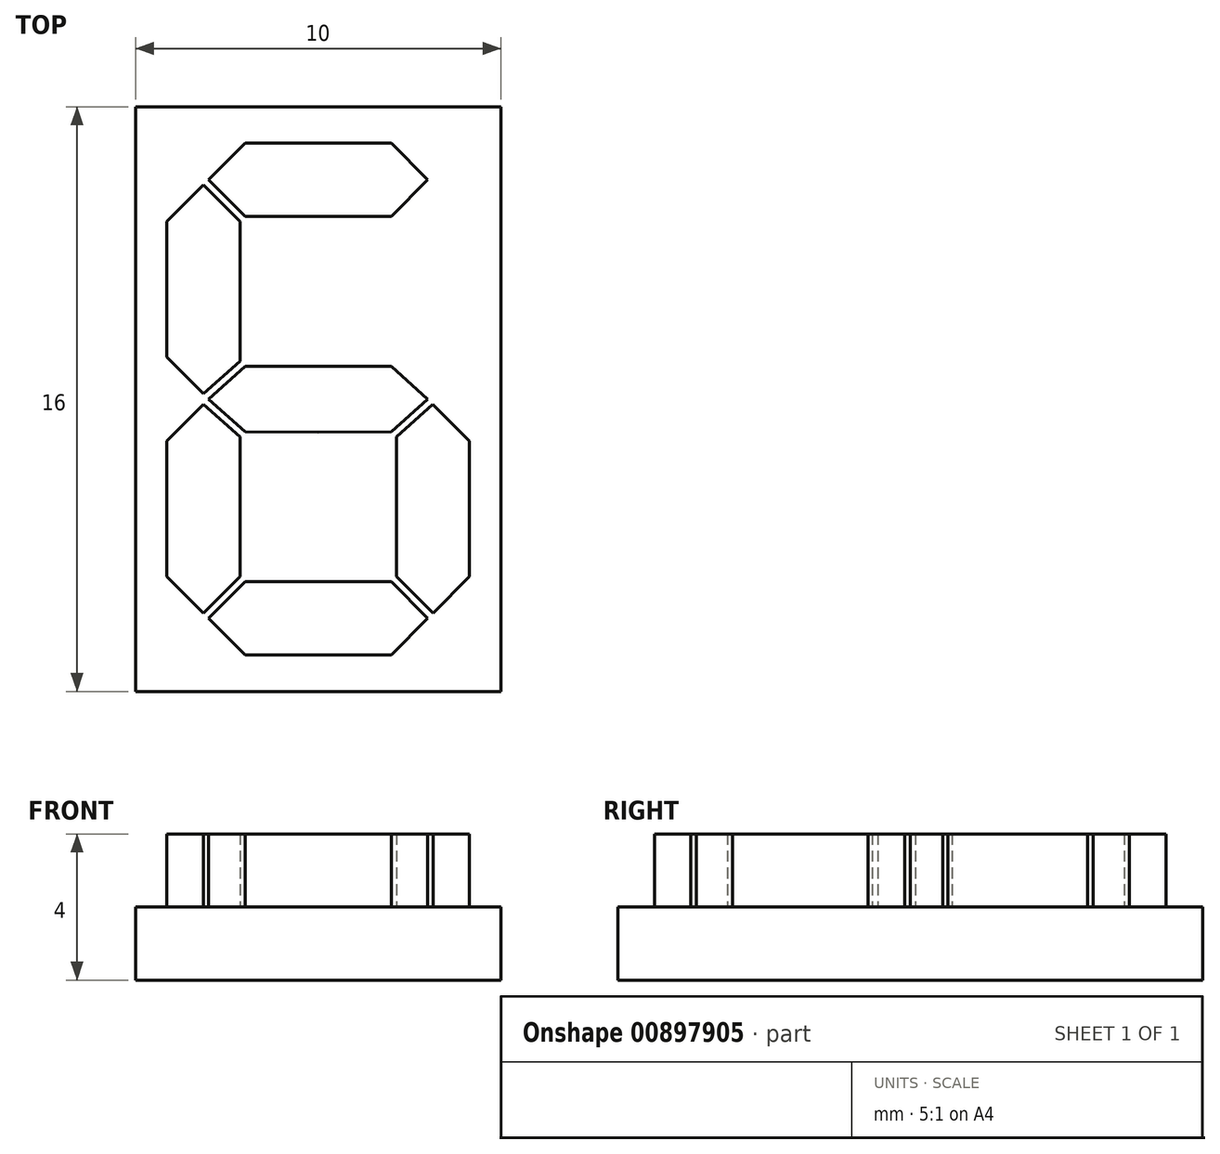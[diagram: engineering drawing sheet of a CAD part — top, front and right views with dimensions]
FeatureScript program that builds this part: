
annotation { "Feature Type Name" : "Feature", "Feature Type Description" : "" }
export const myFeature = defineFeature(function(context is Context, id is Id, definition is map)
    precondition{}
    {
        {
            var Q0;
            Q0=qCreatedBy(makeId("Top.planeOp"),FACE);
            var sketch = newSketch(context, id + "F0", { "sketchPlane" : qUnion([Q0])});
            skLineSegment(sketch, "E0.bottom", {"start": v(5, -8) * mm, "end": v(-5, -8) * mm});
            skLineSegment(sketch, "E0.top", {"start": v(5, 8) * mm, "end": v(-5, 8) * mm});
            skLineSegment(sketch, "E0.left", {"start": v(5, -8) * mm, "end": v(5, 8) * mm});
            skLineSegment(sketch, "E0.right", {"start": v(-5, -8) * mm, "end": v(-5, 8) * mm});
            skPoint(sketch, "E0.middle", {"position": v(0, 0) * mm});
            skSolve(sketch);
        }
        {
            var Q0;
            Q0=makeQuery(id+"F0.imprint","IMPRINT",FACE,{"disambiguationData":[TD([[makeQuery(id+"F0.imprint","IMPRINT",EDGE,{"derivedFrom":sQuery(id+"F0.wireOp",EDGE,"E0.bottom")}),-1.0]])]});
            extrude(context, id + "F1", {"entities" : qUnion([Q0]), "depth" : 2 * mm, "offsetDistance" : 25 * mm});
        }
        {
            var Q0;
            Q0=makeQuery(id+"F1.opExtrude","CAP_FACE",FACE,{"disambiguationData":[OSD([sQuery(id+"F0.wireOp",EDGE,"E0.bottom"),sQuery(id+"F0.wireOp",EDGE,"E0.top"),sQuery(id+"F0.wireOp",EDGE,"E0.left"),sQuery(id+"F0.wireOp",EDGE,"E0.right")])],"isStart":false});
            var sketch = newSketch(context, id + "F2", { "sketchPlane" : qUnion([Q0])});
            skLineSegment(sketch, "E1", {"start": v(-3, 8) * mm, "end": v(-3, -8) * mm, "construction": true});
            skLineSegment(sketch, "E2.0.1.0", {"start": v(-5, 6) * mm, "end": v(5, 6) * mm, "construction": true});
            skLineSegment(sketch, "E2.direction2", {"start": v(-5, 7) * mm, "end": v(-5, 6) * mm, "construction": true});
            skLineSegment(sketch, "E3.1.0.0", {"start": v(-2, 8) * mm, "end": v(-2, -8) * mm, "construction": true});
            skLineSegment(sketch, "E3.3.0.0", {"start": v(0, 8) * mm, "end": v(0, -8) * mm, "construction": true});
            skLineSegment(sketch, "E3.direction1", {"start": v(-3, -8) * mm, "end": v(-2, -8) * mm, "construction": true});
            skLineSegment(sketch, "E4", {"start": v(-2, 7) * mm, "end": v(-3, 6) * mm});
            skLineSegment(sketch, "E5", {"start": v(-3, 6) * mm, "end": v(-2, 5) * mm});
            skLineSegment(sketch, "E6", {"start": v(-2, 5) * mm, "end": v(0, 5) * mm});
            skLineSegment(sketch, "E7", {"start": v(-2, 7) * mm, "end": v(0, 7) * mm});
            skLineSegment(sketch, "E8.0", {"start": v(-3.14, 5.86) * mm, "end": v(-2.14, 4.86) * mm});
            skLineSegment(sketch, "E9", {"start": v(-2.14, 4.86) * mm, "end": v(-2.14, 1.03) * mm});
            skLineSegment(sketch, "E10.0", {"start": v(-4.14, 4.86) * mm, "end": v(-4.14, 1.15) * mm});
            skLineSegment(sketch, "E11", {"start": v(-3.14, 5.86) * mm, "end": v(-4.14, 4.86) * mm});
            skLineSegment(sketch, "E12", {"start": v(-4.14, 4.86) * mm, "end": v(5, 4.86) * mm, "construction": true});
            skLineSegment(sketch, "E13", {"start": v(0, 0.9) * mm, "end": v(-2, 0.9) * mm});
            skLineSegment(sketch, "E14", {"start": v(-2, 0.9) * mm, "end": v(-3, 0) * mm});
            skLineSegment(sketch, "E15.0", {"start": v(-2.14, 1.03) * mm, "end": v(-3.14, 0.15) * mm});
            skLineSegment(sketch, "E16", {"start": v(-3.14, 5.86) * mm, "end": v(-3.14, 0.15) * mm, "construction": true});
            skLineSegment(sketch, "E17", {"start": v(-4.14, 1.15) * mm, "end": v(-3.14, 0.15) * mm});
            skLineSegment(sketch, "E18.MirrorCS", {"start": v(0, -0.9) * mm, "end": v(-2, -0.9) * mm});
            skLineSegment(sketch, "E19.MirrorCS", {"start": v(-2, -0.9) * mm, "end": v(-3, 0) * mm});
            skLineSegment(sketch, "E20.MirrorCS", {"start": v(-2, -5) * mm, "end": v(0, -5) * mm});
            skLineSegment(sketch, "E21.MirrorCS", {"start": v(-3, -6) * mm, "end": v(-2, -5) * mm});
            skLineSegment(sketch, "E22.MirrorCS", {"start": v(-2, -7) * mm, "end": v(-3, -6) * mm});
            skLineSegment(sketch, "E23.MirrorCS", {"start": v(-2, -7) * mm, "end": v(0, -7) * mm});
            skLineSegment(sketch, "E24.MirrorCS", {"start": v(-3.14, -5.86) * mm, "end": v(-2.14, -4.86) * mm});
            skLineSegment(sketch, "E25.MirrorCS", {"start": v(-3.14, -5.86) * mm, "end": v(-4.14, -4.86) * mm});
            skLineSegment(sketch, "E26.MirrorCS", {"start": v(-4.14, -4.86) * mm, "end": v(-4.14, -1.15) * mm});
            skLineSegment(sketch, "E27.MirrorCS", {"start": v(-4.14, -1.15) * mm, "end": v(-3.14, -0.15) * mm});
            skLineSegment(sketch, "E28.MirrorCS", {"start": v(-2.14, -4.86) * mm, "end": v(-2.14, -1.03) * mm});
            skLineSegment(sketch, "E29.MirrorCS", {"start": v(-2.14, -1.03) * mm, "end": v(-3.14, -0.15) * mm});
            skLineSegment(sketch, "E30.MirrorCS", {"start": v(2, 7) * mm, "end": v(0, 7) * mm});
            skLineSegment(sketch, "E31.MirrorCS", {"start": v(2, 7) * mm, "end": v(3, 6) * mm});
            skLineSegment(sketch, "E32.MirrorCS", {"start": v(3, 6) * mm, "end": v(2, 5) * mm});
            skLineSegment(sketch, "E33.MirrorCS", {"start": v(2, 5) * mm, "end": v(0, 5) * mm});
            skLineSegment(sketch, "E34.MirrorCS", {"start": v(2, 0.9) * mm, "end": v(3, 0) * mm});
            skLineSegment(sketch, "E35.MirrorCS", {"start": v(0, 0.9) * mm, "end": v(2, 0.9) * mm});
            skLineSegment(sketch, "E36.MirrorCS", {"start": v(2, -0.9) * mm, "end": v(3, 0) * mm});
            skLineSegment(sketch, "E37.MirrorCS", {"start": v(0, -0.9) * mm, "end": v(2, -0.9) * mm});
            skLineSegment(sketch, "E38.MirrorCS", {"start": v(2.14, -1.03) * mm, "end": v(3.14, -0.15) * mm});
            skLineSegment(sketch, "E39.MirrorCS", {"start": v(4.14, -1.15) * mm, "end": v(3.14, -0.15) * mm});
            skLineSegment(sketch, "E40.MirrorCS", {"start": v(4.14, -4.86) * mm, "end": v(4.14, -1.15) * mm});
            skLineSegment(sketch, "E41.MirrorCS", {"start": v(2.14, -4.86) * mm, "end": v(2.14, -1.03) * mm});
            skLineSegment(sketch, "E42.MirrorCS", {"start": v(3.14, -5.86) * mm, "end": v(2.14, -4.86) * mm});
            skLineSegment(sketch, "E43.MirrorCS", {"start": v(3.14, -5.86) * mm, "end": v(4.14, -4.86) * mm});
            skLineSegment(sketch, "E44.MirrorCS", {"start": v(3, -6) * mm, "end": v(2, -5) * mm});
            skLineSegment(sketch, "E45.MirrorCS", {"start": v(2, -5) * mm, "end": v(0, -5) * mm});
            skLineSegment(sketch, "E46.MirrorCS", {"start": v(2, -7) * mm, "end": v(3, -6) * mm});
            skLineSegment(sketch, "E47.MirrorCS", {"start": v(2, -7) * mm, "end": v(0, -7) * mm});
            skSolve(sketch);
        }
        {
            var Q0;
            Q0=qSketchRegion(id+"F2",true);
            extrude(context, id + "F3", {"entities" : qUnion([Q0]), "operationType" : NewBodyOperationType.ADD, "depth" : 2 * mm, "offsetDistance" : 25 * mm});
        }
    });
